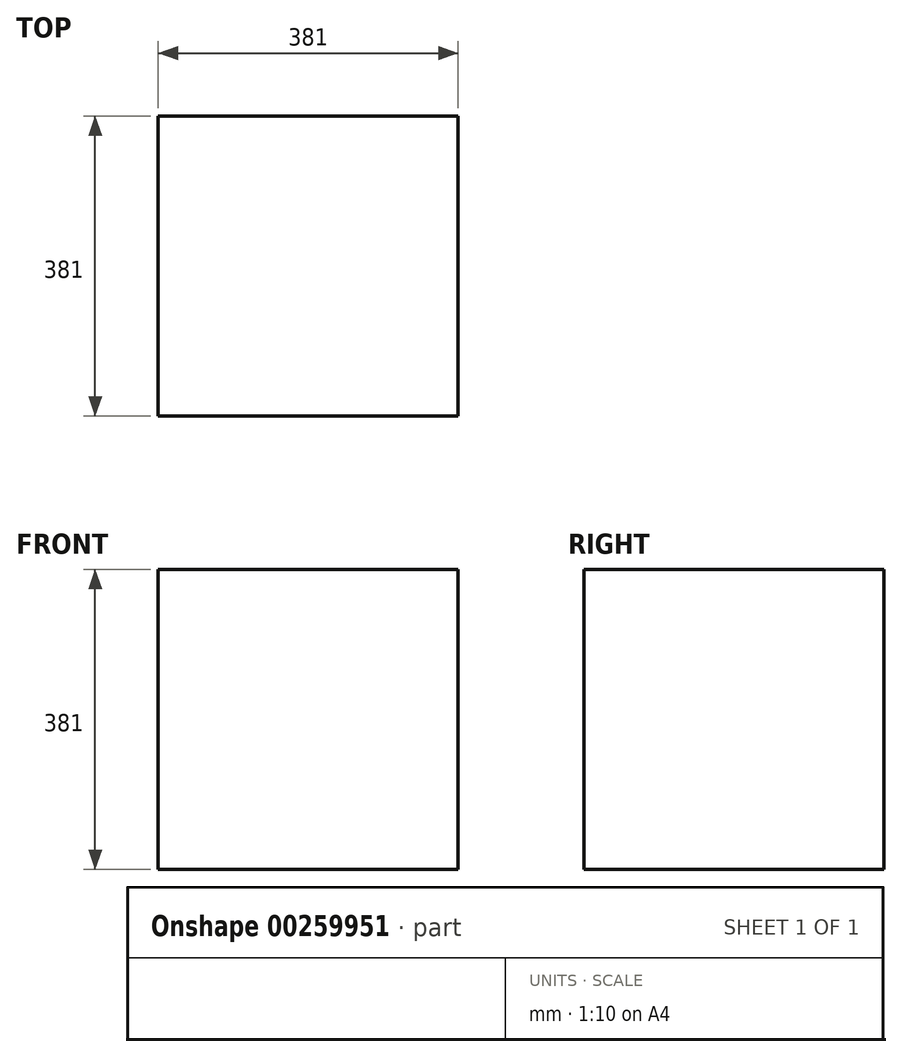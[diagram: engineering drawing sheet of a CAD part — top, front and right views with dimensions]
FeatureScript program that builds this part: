
annotation { "Feature Type Name" : "Feature", "Feature Type Description" : "" }
export const myFeature = defineFeature(function(context is Context, id is Id, definition is map)
    precondition{}
    {
        {
            var Q0;
            Q0=qCreatedBy(makeId("Front.planeOp"),FACE);
            var sketch = newSketch(context, id + "F0", { "sketchPlane" : qUnion([Q0])});
            skLineSegment(sketch, "E0.bottom", {"start": v(190.5, -190.5) * mm, "end": v(-190.5, -190.5) * mm});
            skLineSegment(sketch, "E0.top", {"start": v(190.5, 190.5) * mm, "end": v(-190.5, 190.5) * mm});
            skLineSegment(sketch, "E0.left", {"start": v(190.5, -190.5) * mm, "end": v(190.5, 190.5) * mm});
            skLineSegment(sketch, "E0.right", {"start": v(-190.5, -190.5) * mm, "end": v(-190.5, 190.5) * mm});
            skPoint(sketch, "E0.middle", {"position": v(0, 0) * mm});
            skSolve(sketch);
        }
        {
            var Q0;
            Q0=makeQuery(id+"F0.imprint","IMPRINT",FACE,{"disambiguationData":[TD([[makeQuery(id+"F0.imprint","IMPRINT",EDGE,{"derivedFrom":sQuery(id+"F0.wireOp",EDGE,"E0.bottom")}),-1.0]])]});
            extrude(context, id + "F1", {"entities" : qUnion([Q0]), "depth" : 381 * mm});
        }
    });
